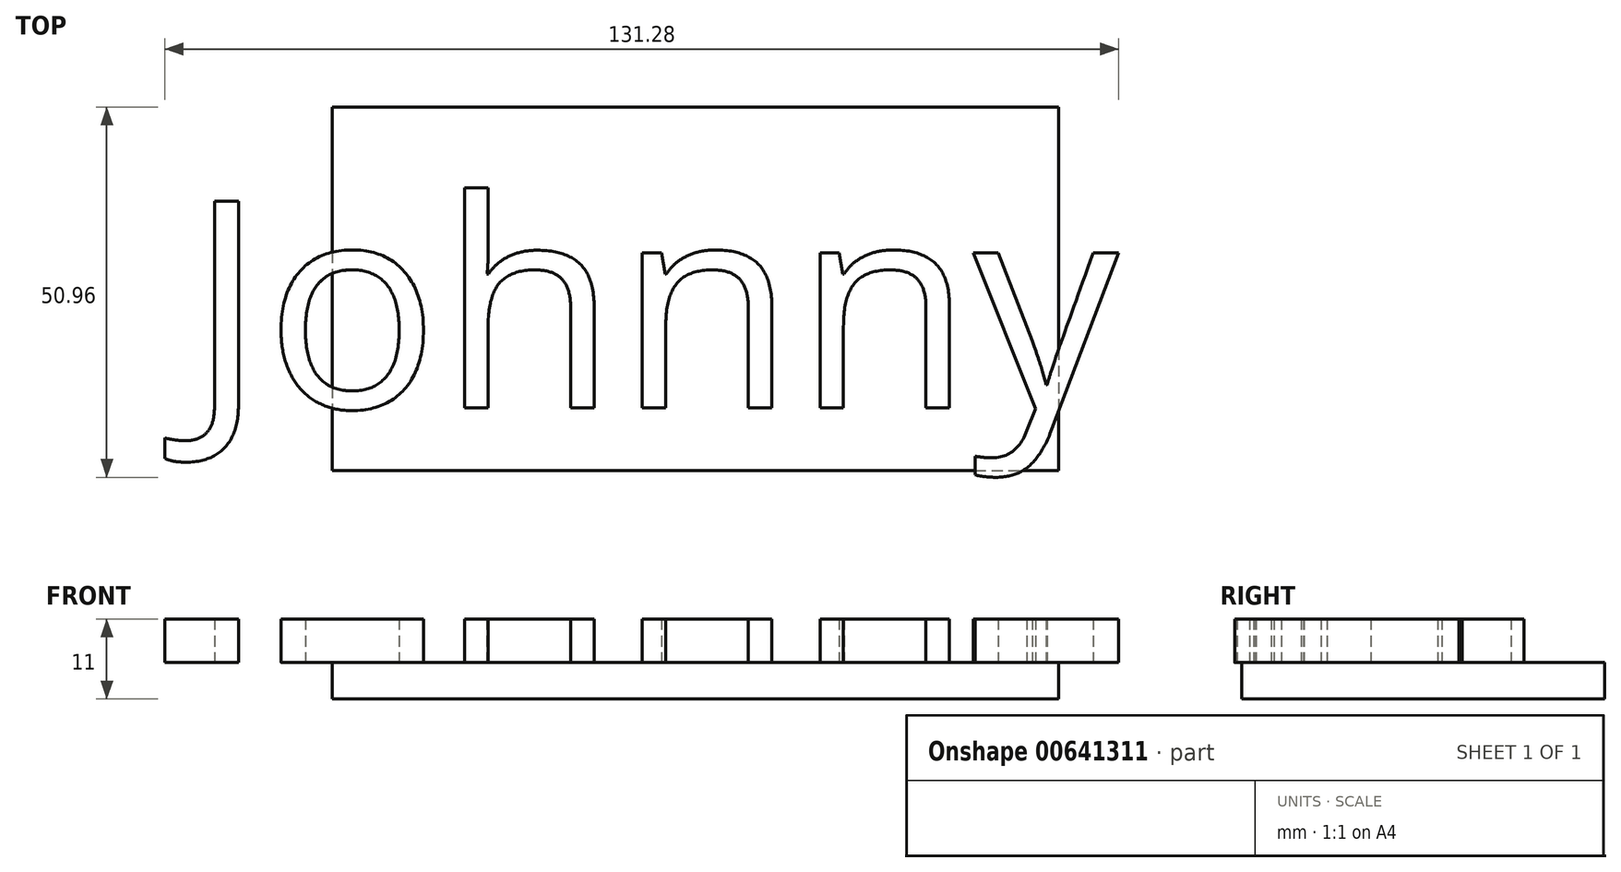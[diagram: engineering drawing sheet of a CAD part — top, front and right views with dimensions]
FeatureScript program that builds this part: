
annotation { "Feature Type Name" : "Feature", "Feature Type Description" : "" }
export const myFeature = defineFeature(function(context is Context, id is Id, definition is map)
    precondition{}
    {
        {
            var Q0;
            Q0=qCreatedBy(makeId("Top.planeOp"),FACE);
            var sketch = newSketch(context, id + "F0", { "sketchPlane" : qUnion([Q0])});
            skLineSegment(sketch, "E0.bottom", {"start": v(-24.54, 17.3) * mm, "end": v(75.46, 17.3) * mm});
            skLineSegment(sketch, "E0.top", {"start": v(-24.54, -32.7) * mm, "end": v(75.46, -32.7) * mm});
            skLineSegment(sketch, "E0.left", {"start": v(-24.54, 17.3) * mm, "end": v(-24.54, -32.7) * mm});
            skLineSegment(sketch, "E0.right", {"start": v(75.46, 17.3) * mm, "end": v(75.46, -32.7) * mm});
            skSolve(sketch);
        }
        {
            var Q0;
            Q0 = qSketchRegion(id + "F0", true);
            extrude(context, id + "F1", {"entities" : qUnion([Q0]), "depth" : 5 * mm, "offsetDistance" : 25 * mm});
        }
        {
            var Q0;
            Q0 = qSketchRegion(id + "F0", true);
            extrude(context, id + "F2", {"entities" : qUnion([Q0]), "operationType" : NewBodyOperationType.ADD, "depth" : 5 * mm, "offsetDistance" : 25 * mm});
        }
        {
            var Q0;
            Q0=makeQuery(id+"F1.opExtrude","CAP_FACE",FACE,{"disambiguationData":[OSD([sQuery(id+"F0.wireOp",EDGE,"E0.bottom"),sQuery(id+"F0.wireOp",EDGE,"E0.top"),sQuery(id+"F0.wireOp",EDGE,"E0.left"),sQuery(id+"F0.wireOp",EDGE,"E0.right")])],"isStart":false});
            var sketch = newSketch(context, id + "F3", { "sketchPlane" : qUnion([Q0])});
            skText(sketch, "E1", { "text": "Johnny", "fontName": "OpenSans-Regular.ttf"});
            const initialGuessF3  = {"E1": [-0.04448, -0.02408, 1, 0, 0.0287]};
            skSetInitialGuess(sketch, initialGuessF3);
            skSolve(sketch);
        }
        {
            var Q0;
            Q0 = qSketchRegion(id + "F3", true);
            extrude(context, id + "F4", {"entities" : qUnion([Q0]), "operationType" : NewBodyOperationType.ADD, "depth" : 6 * mm, "offsetDistance" : 25 * mm});
        }
    });
